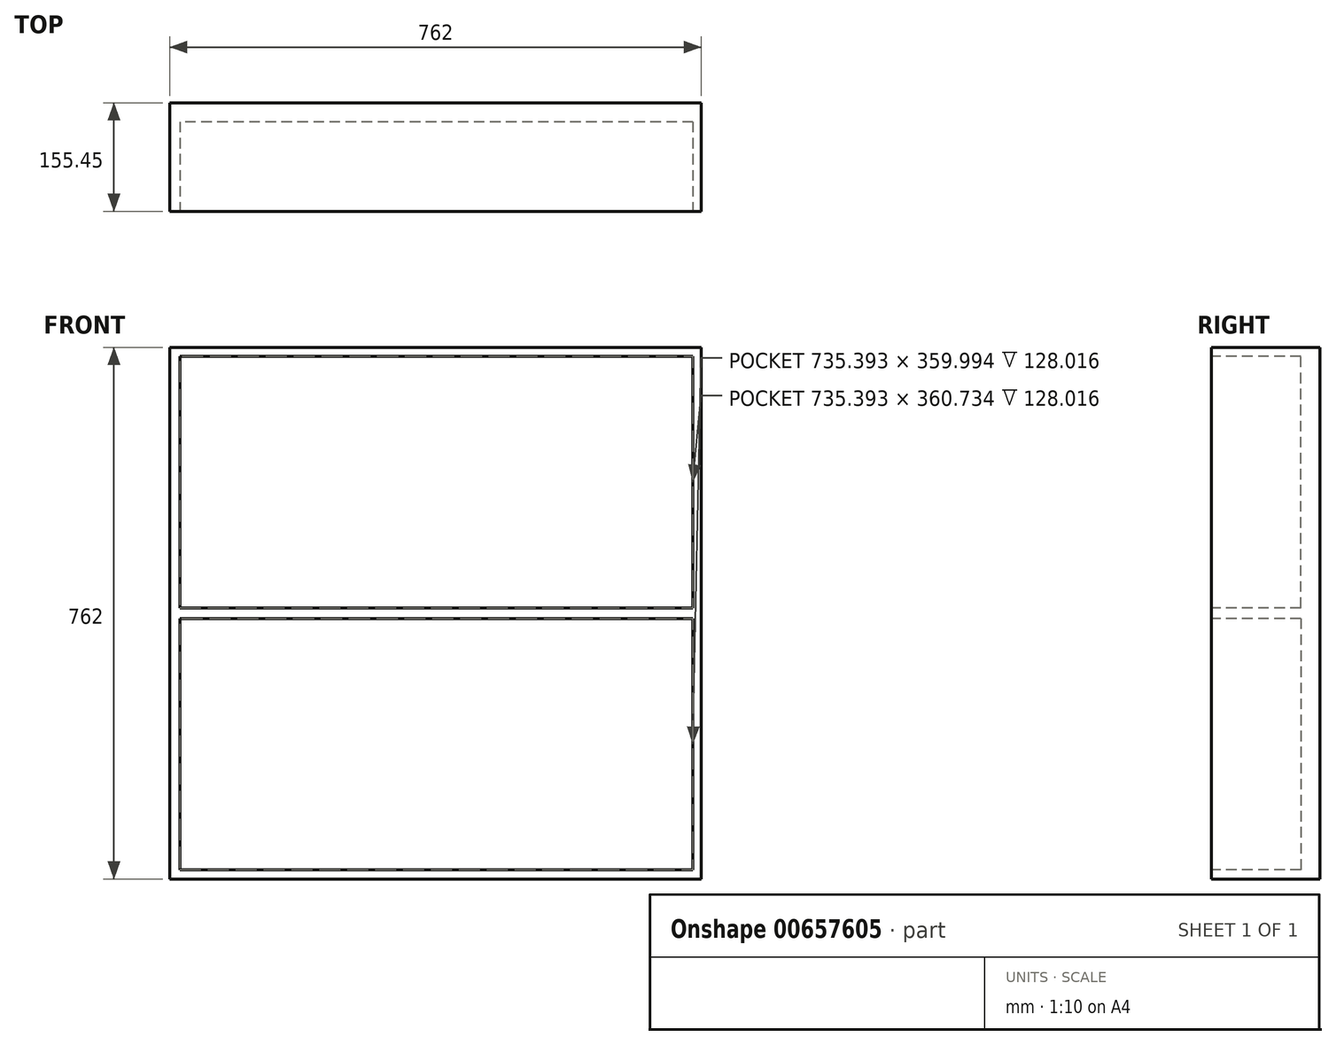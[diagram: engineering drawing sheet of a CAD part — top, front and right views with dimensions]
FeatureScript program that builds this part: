
annotation { "Feature Type Name" : "Feature", "Feature Type Description" : "" }
export const myFeature = defineFeature(function(context is Context, id is Id, definition is map)
    precondition{}
    {
        {
            var Q0;
            Q0=qCreatedBy(makeId("Front.planeOp"),FACE);
            var sketch = newSketch(context, id + "F0", { "sketchPlane" : qUnion([Q0])});
            skLineSegment(sketch, "E0.bottom", {"start": v(0, 0) * mm, "end": v(-762, 0) * mm});
            skLineSegment(sketch, "E0.top", {"start": v(0, 762) * mm, "end": v(-762, 762) * mm});
            skLineSegment(sketch, "E0.left", {"start": v(0, 0) * mm, "end": v(0, 762) * mm});
            skLineSegment(sketch, "E0.right", {"start": v(-762, 0) * mm, "end": v(-762, 762) * mm});
            skSolve(sketch);
        }
        {
            var Q0;
            Q0=makeQuery(id+"F0.imprint","IMPRINT",FACE,{"disambiguationData":[TD([[makeQuery(id+"F0.imprint","IMPRINT",EDGE,{"derivedFrom":sQuery(id+"F0.wireOp",EDGE,"E0.bottom")}),-1.0]])]});
            extrude(context, id + "F1", {"entities" : qUnion([Q0]), "depth" : 155.45 * mm, "offsetDistance" : 30.48 * mm});
        }
        {
            var Q0;
            Q0=makeQuery(id+"F1.opExtrude","CAP_FACE",FACE,{"disambiguationData":[OSD([sQuery(id+"F0.wireOp",EDGE,"E0.bottom"),sQuery(id+"F0.wireOp",EDGE,"E0.top"),sQuery(id+"F0.wireOp",EDGE,"E0.left"),sQuery(id+"F0.wireOp",EDGE,"E0.right")])],"isStart":false});
            var sketch = newSketch(context, id + "F2", { "sketchPlane" : qUnion([Q0])});
            skPoint(sketch, "E1", {"position": v(-381, 388.62) * mm});
            skPoint(sketch, "E2", {"position": v(-381, 373.38) * mm});
            skLineSegment(sketch, "E3", {"start": v(-381, 388.62) * mm, "end": v(-762, 388.62) * mm});
            skLineSegment(sketch, "E4", {"start": v(-762, 388.62) * mm, "end": v(0, 388.62) * mm});
            skLineSegment(sketch, "E5", {"start": v(-381, 373.38) * mm, "end": v(-762, 373.38) * mm});
            skLineSegment(sketch, "E6", {"start": v(-762, 373.38) * mm, "end": v(0, 373.38) * mm});
            skLineSegment(sketch, "E7.bottom", {"start": v(-747.25, 388.62) * mm, "end": v(-11.86, 388.62) * mm});
            skLineSegment(sketch, "E7.top", {"start": v(-747.25, 749.35) * mm, "end": v(-11.86, 749.35) * mm});
            skLineSegment(sketch, "E7.left", {"start": v(-747.25, 388.62) * mm, "end": v(-747.25, 749.35) * mm});
            skLineSegment(sketch, "E7.right", {"start": v(-11.86, 388.62) * mm, "end": v(-11.86, 749.35) * mm});
            skLineSegment(sketch, "E8.bottom", {"start": v(-747.25, 373.38) * mm, "end": v(-11.86, 373.38) * mm});
            skLineSegment(sketch, "E8.top", {"start": v(-747.25, 13.39) * mm, "end": v(-11.86, 13.39) * mm});
            skLineSegment(sketch, "E8.left", {"start": v(-747.25, 373.38) * mm, "end": v(-747.25, 13.39) * mm});
            skLineSegment(sketch, "E8.right", {"start": v(-11.86, 373.38) * mm, "end": v(-11.86, 13.39) * mm});
            skSolve(sketch);
        }
        {
            var Q0;
            Q0=makeQuery(id+"F2.imprint","IMPRINT",FACE,{"disambiguationData":[TD([[makeQuery(id+"F2.imprint","IMPRINT",EDGE,{"derivedFrom":sQuery(id+"F2.wireOp",EDGE,"E7.top")}),-1.0]])]});
            var Q1;
            Q1=makeQuery(id+"F2.imprint","IMPRINT",FACE,{"disambiguationData":[TD([[makeQuery(id+"F2.imprint","IMPRINT",EDGE,{"derivedFrom":sQuery(id+"F2.wireOp",EDGE,"E8.top")}),1.0]])]});
            extrude(context, id + "F3", {"entities" : qUnion([Q0, Q1]), "operationType" : NewBodyOperationType.REMOVE, "oppositeDirection" : true, "depth" : 128.02 * mm, "offsetDistance" : 30.48 * mm});
        }
    });
